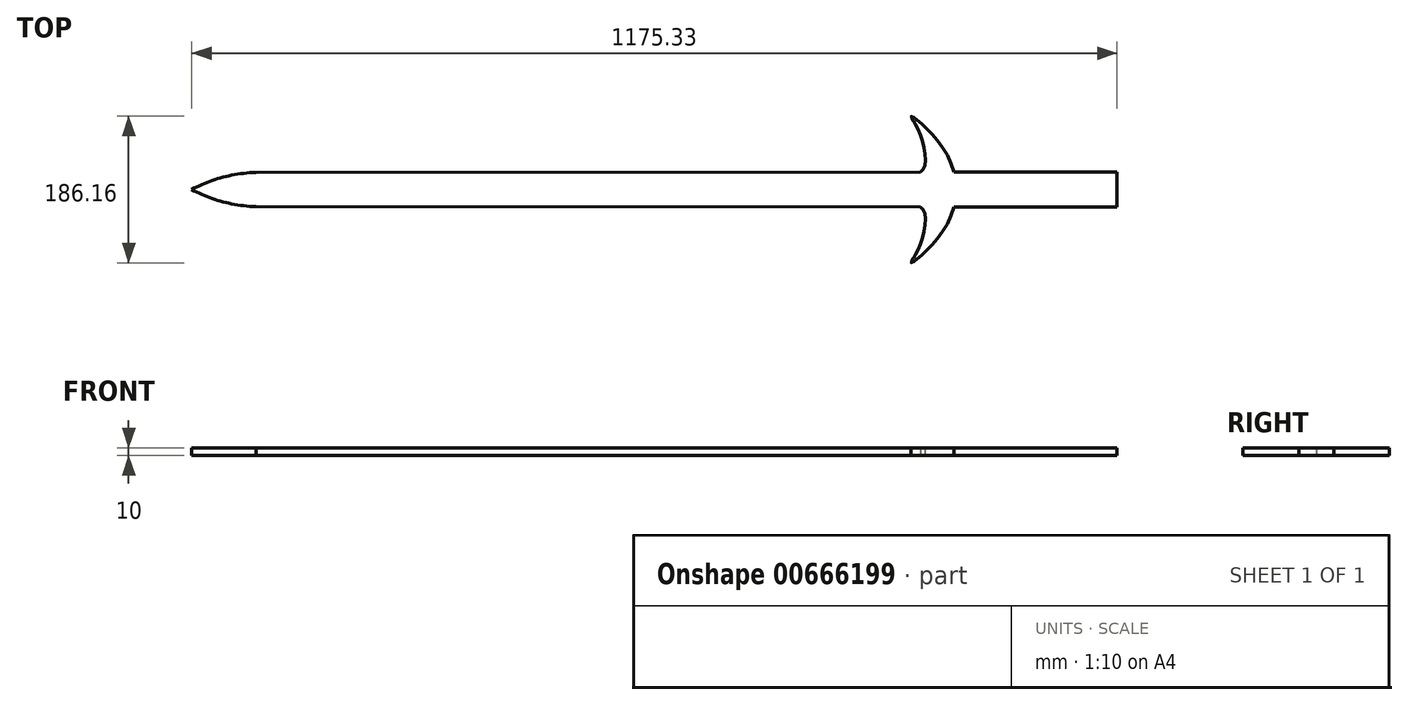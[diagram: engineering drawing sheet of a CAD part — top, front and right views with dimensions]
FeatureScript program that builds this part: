
annotation { "Feature Type Name" : "Feature", "Feature Type Description" : "" }
export const myFeature = defineFeature(function(context is Context, id is Id, definition is map)
    precondition{}
    {
        {
            var Q0;
            Q0=qCreatedBy(makeId("Top.planeOp"),FACE);
            var sketch = newSketch(context, id + "F0", { "sketchPlane" : qUnion([Q0])});
            skLineSegment(sketch, "E0", {"start": v(0, 0) * mm, "end": v(-461.18, 0) * mm, "construction": true});
            skLineSegment(sketch, "E1", {"start": v(-496.4, 21.99) * mm, "end": v(-703.58, 21.95) * mm});
            skFitSpline(sketch, "E2", {"points": [v(-1590.17, 21.8) * mm, v(-1671.72, 0) * mm], "startDerivative": vector(-94.73, -3.64) * mm, "endDerivative": vector(-72.07, -38.37) * mm});
            skFitSpline(sketch, "E3", {"points": [v(-703.58, 21.95) * mm, v(-757.8, 93.07) * mm, v(-749.45, 77.27) * mm, v(-746.2, 21.94) * mm], "startDerivative": vector(-64.8, 259.19) * mm, "endDerivative": vector(-99.78, -56.7) * mm});
            skLineSegment(sketch, "E4.trimOffspring", {"start": v(-746.2, 21.94) * mm, "end": v(-1590.17, 21.8) * mm});
            skFitSpline(sketch, "E5.MirrorCS", {"points": [v(-1590.17, -21.8) * mm, v(-1671.72, 0) * mm], "startDerivative": vector(-94.73, 3.64) * mm, "endDerivative": vector(-72.07, 38.37) * mm});
            skFitSpline(sketch, "E6.MirrorCS", {"points": [v(-703.58, -21.95) * mm, v(-757.8, -93.07) * mm, v(-749.45, -77.27) * mm, v(-746.2, -21.94) * mm], "startDerivative": vector(-64.8, -259.19) * mm, "endDerivative": vector(-99.78, 56.7) * mm});
            skLineSegment(sketch, "E7.MirrorCS", {"start": v(-746.2, -21.94) * mm, "end": v(-1590.17, -21.8) * mm});
            skLineSegment(sketch, "E8.MirrorCS", {"start": v(-496.4, -21.99) * mm, "end": v(-703.58, -21.95) * mm});
            skLineSegment(sketch, "E9", {"start": v(-496.4, 21.99) * mm, "end": v(-496.4, -21.99) * mm});
            skLineSegment(sketch, "E10", {"start": v(-746.2, 21.94) * mm, "end": v(-746.2, -21.94) * mm});
            skLineSegment(sketch, "E11", {"start": v(-703.58, -21.95) * mm, "end": v(-703.58, 21.95) * mm});
            skLineSegment(sketch, "E12", {"start": v(-1671.72, 0) * mm, "end": v(-746.2, 0.16) * mm});
            skSolve(sketch);
        }
        {
            var Q0;
            Q0=makeQuery(id+"F0.imprint","IMPRINT",FACE,{"disambiguationData":[TD([[makeQuery(id+"F0.imprint","IMPRINT",EDGE,{"derivedFrom":sQuery(id+"F0.wireOp",EDGE,"E5.MirrorCS")}),-1.0]])]});
            var Q1;
            Q1=makeQuery(id+"F0.imprint","IMPRINT",FACE,{"disambiguationData":[TD([[makeQuery(id+"F0.imprint","IMPRINT",EDGE,{"derivedFrom":sQuery(id+"F0.wireOp",EDGE,"E2")}),1.0]])]});
            var Q2;
            {var subQ1=sQuery(id+"F0.wireOp",EDGE,"E3");Q2=makeQuery(id+"F0.imprint","IMPRINT",FACE,{"disambiguationData":[TD([[makeQuery(id+"F0.imprint","IMPRINT",EDGE,{"derivedFrom":subQ1}),1.0]])]});}
            var Q3;
            Q3=makeQuery(id+"F0.imprint","IMPRINT",FACE,{"disambiguationData":[TD([[makeQuery(id+"F0.imprint","IMPRINT",EDGE,{"derivedFrom":sQuery(id+"F0.wireOp",EDGE,"E1")}),1.0]])]});
            extrude(context, id + "F1", {"entities" : qUnion([Q0, Q1, Q2, Q3]), "depth" : 10 * mm, "offsetDistance" : 25 * mm});
        }
    });
